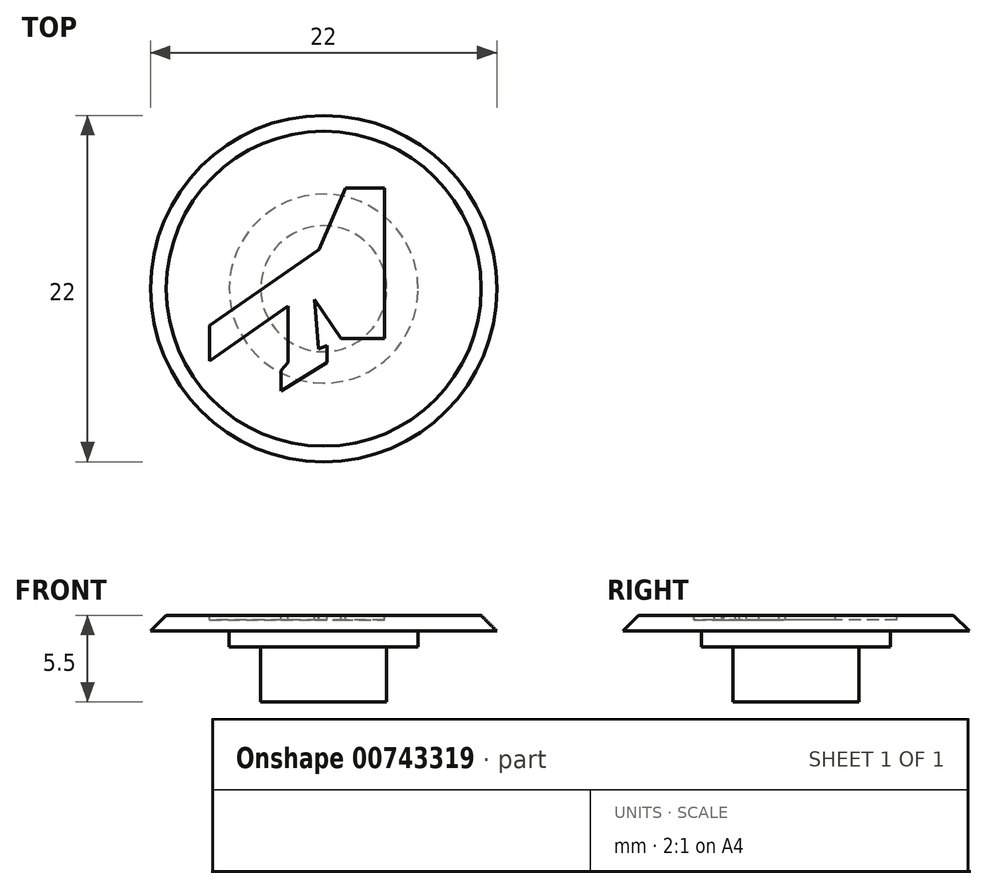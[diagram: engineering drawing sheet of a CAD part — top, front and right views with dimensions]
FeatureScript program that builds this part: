
annotation { "Feature Type Name" : "Feature", "Feature Type Description" : "" }
export const myFeature = defineFeature(function(context is Context, id is Id, definition is map)
    precondition{}
    {
        {
            var Q0;
            Q0=qCreatedBy(makeId("Top.planeOp"),FACE);
            var sketch = newSketch(context, id + "F0", { "sketchPlane" : qUnion([Q0])});
            skCircle(sketch, "E0", {"center": v(0, 0) * mm, "radius": 4 * mm});
            skSolve(sketch);
        }
        {
            var Q0;
            Q0=makeQuery(id+"F0.imprint","IMPRINT",FACE,{"disambiguationData":[TD([[makeQuery(id+"F0.imprint","IMPRINT",EDGE,{"derivedFrom":sQuery(id+"F0.wireOp",EDGE,"E0")}),1.0]])]});
            extrude(context, id + "F1", {"entities" : qUnion([Q0]), "depth" : 3.5 * mm, "offsetDistance" : 25 * mm});
        }
        {
            var Q0;
            Q0=makeQuery(id+"F1.opExtrude","CAP_FACE",FACE,{"disambiguationData":[OSD([sQuery(id+"F0.wireOp",EDGE,"E0")])],"isStart":false});
            var sketch = newSketch(context, id + "F2", { "sketchPlane" : qUnion([Q0])});
            skCircle(sketch, "E1", {"center": v(0, 0) * mm, "radius": 6 * mm});
            skSolve(sketch);
        }
        {
            var Q0;
            Q0=qSketchRegion(id+"F2",true);
            extrude(context, id + "F3", {"entities" : qUnion([Q0]), "operationType" : NewBodyOperationType.ADD, "depth" : 1 * mm, "offsetDistance" : 25 * mm});
        }
        {
            var Q0;
            Q0=makeQuery(id+"F3.opExtrude","CAP_FACE",FACE,{"disambiguationData":[OSD([sQuery(id+"F2.wireOp",EDGE,"E1")])],"isStart":false});
            var sketch = newSketch(context, id + "F4", { "sketchPlane" : qUnion([Q0])});
            skCircle(sketch, "E2", {"center": v(0, 0) * mm, "radius": 11 * mm});
            skSolve(sketch);
        }
        {
            var Q0;
            Q0=qSketchRegion(id+"F4",true);
            extrude(context, id + "F5", {"entities" : qUnion([Q0]), "operationType" : NewBodyOperationType.ADD, "depth" : 1 * mm, "offsetDistance" : 25 * mm});
        }
        {
            var Q0;
            Q0=makeQuery(id+"F5.opExtrude","CAP_EDGE",EDGE,{"disambiguationData":[OSD([sQuery(id+"F4.wireOp",EDGE,"E2")])],"isStart":false});
            chamfer(context, id + "F6", {"entities" : qUnion([Q0]), "width" : 1 * mm, "tangentPropagation" : true});
        }
        {
            var Q0;
            Q0=makeQuery(id+"F5.opExtrude","CAP_FACE",FACE,{"disambiguationData":[OSD([sQuery(id+"F4.wireOp",EDGE,"E2")])],"isStart":false});
            var sketch = newSketch(context, id + "F7", { "sketchPlane" : qUnion([Q0])});
            skLineSegment(sketch, "E3", {"start": v(-0.3, 2.5) * mm, "end": v(-7.24, -2.35) * mm});
            skLineSegment(sketch, "E4", {"start": v(-7.24, -2.35) * mm, "end": v(-7.24, -4.58) * mm});
            skLineSegment(sketch, "E5", {"start": v(-7.24, -4.58) * mm, "end": v(-2.27, -1.09) * mm});
            skLineSegment(sketch, "E6", {"start": v(-2.27, -1.09) * mm, "end": v(-2.27, -4.7) * mm});
            skLineSegment(sketch, "E7", {"start": v(-2.27, -4.7) * mm, "end": v(-2.7, -5.19) * mm});
            skLineSegment(sketch, "E8", {"start": v(-2.7, -5.19) * mm, "end": v(-2.7, -6.48) * mm});
            skLineSegment(sketch, "E9", {"start": v(-2.7, -6.48) * mm, "end": v(0.2, -4.7) * mm});
            skLineSegment(sketch, "E10", {"start": v(0.2, -4.7) * mm, "end": v(0.2, -3.6) * mm});
            skLineSegment(sketch, "E11", {"start": v(0.2, -3.6) * mm, "end": v(-0.33, -3.84) * mm});
            skLineSegment(sketch, "E12", {"start": v(-0.33, -3.84) * mm, "end": v(-0.57, -0.68) * mm});
            skLineSegment(sketch, "E13", {"start": v(-0.57, -0.68) * mm, "end": v(1.1, -3.16) * mm});
            skLineSegment(sketch, "E14", {"start": v(1.1, -3.16) * mm, "end": v(2.47, -3.16) * mm});
            skLineSegment(sketch, "E15", {"start": v(2.47, -3.16) * mm, "end": v(3.85, -3.16) * mm});
            skLineSegment(sketch, "E16", {"start": v(3.85, -3.16) * mm, "end": v(3.85, -3.65) * mm});
            skLineSegment(sketch, "E17", {"start": v(3.85, -3.65) * mm, "end": v(3.85, 4.69) * mm});
            skLineSegment(sketch, "E18", {"start": v(3.85, 43.27) * mm, "end": v(3.85, 4.69) * mm});
            skLineSegment(sketch, "E19", {"start": v(3.85, 43.27) * mm, "end": v(3.85, -6.35) * mm});
            skLineSegment(sketch, "E20", {"start": v(3.85, -6.35) * mm, "end": v(3.85, -5.22) * mm});
            skLineSegment(sketch, "E21", {"start": v(3.85, -5.22) * mm, "end": v(5.68, -4.7) * mm});
            skLineSegment(sketch, "E22", {"start": v(5.68, -4.7) * mm, "end": v(5.93, -0.36) * mm});
            skLineSegment(sketch, "E23", {"start": v(5.93, -0.36) * mm, "end": v(6.56, -0.4) * mm});
            skLineSegment(sketch, "E24", {"start": v(6.56, -0.4) * mm, "end": v(6.56, 0.83) * mm});
            skLineSegment(sketch, "E25", {"start": v(6.56, 0.83) * mm, "end": v(5.12, 6.4) * mm});
            skLineSegment(sketch, "E26", {"start": v(5.12, 6.4) * mm, "end": v(1.37, 6.4) * mm});
            skLineSegment(sketch, "E27", {"start": v(1.37, 6.4) * mm, "end": v(-0.3, 2.5) * mm});
            skSolve(sketch);
        }
        {
            var Q0;
            Q0=makeQuery(id+"F7.imprint","IMPRINT",FACE,{"disambiguationData":[TD([[makeQuery(id+"F7.imprint","IMPRINT",EDGE,{"derivedFrom":sQuery(id+"F7.wireOp",EDGE,"E3")}),1.0]])]});
            extrude(context, id + "F8", {"entities" : qUnion([Q0]), "operationType" : NewBodyOperationType.REMOVE, "depth" : -.3 * mm, "offsetDistance" : 25 * mm});
        }
    });
